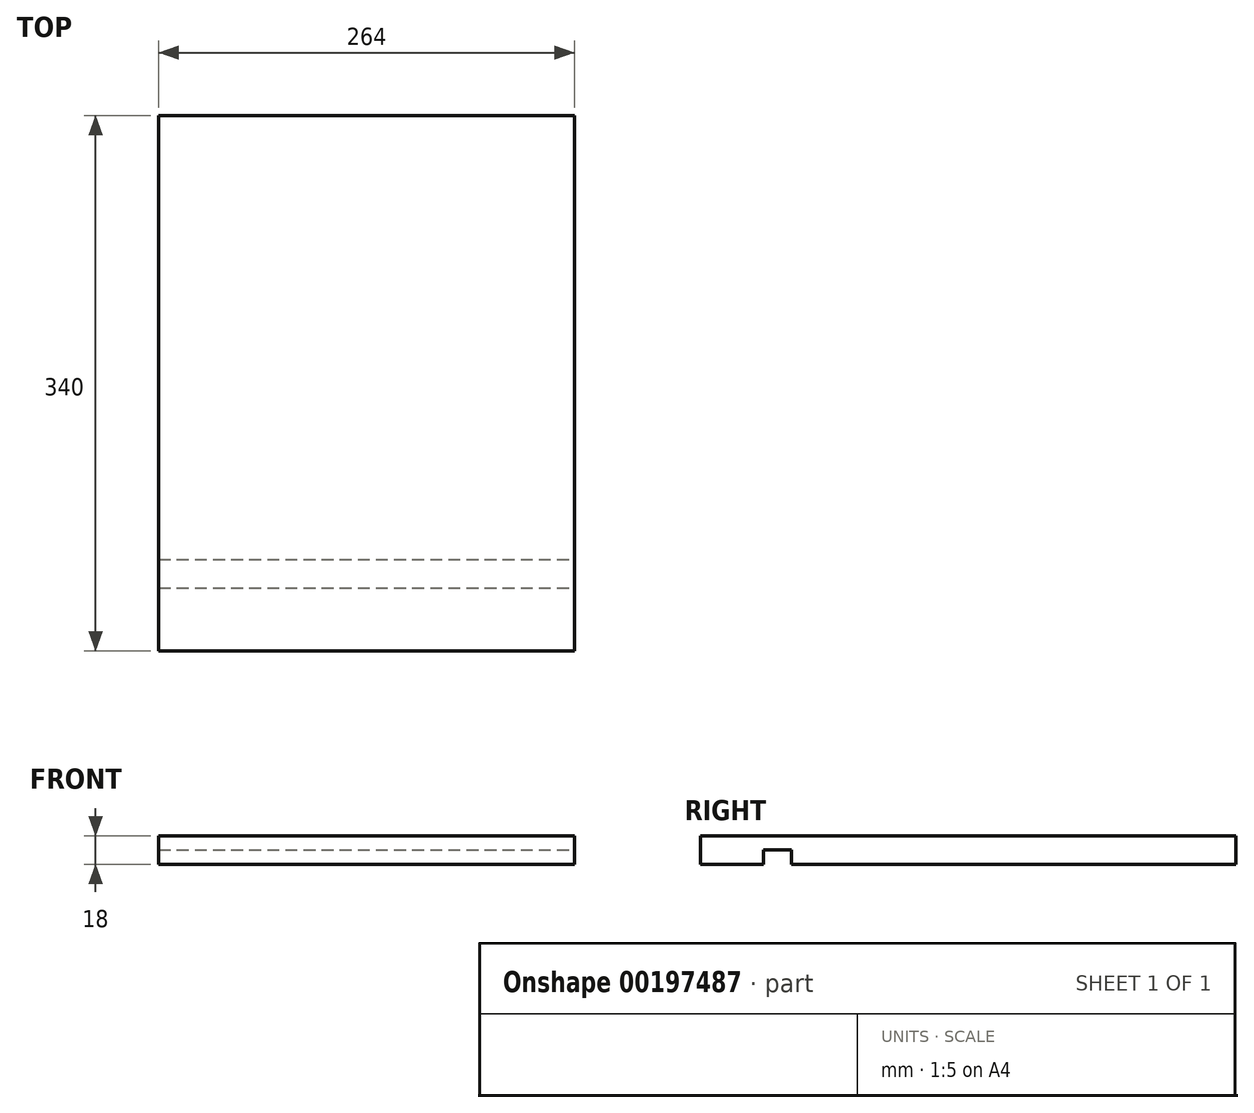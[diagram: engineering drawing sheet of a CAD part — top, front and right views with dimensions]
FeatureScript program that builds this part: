
annotation { "Feature Type Name" : "Feature", "Feature Type Description" : "" }
export const myFeature = defineFeature(function(context is Context, id is Id, definition is map)
    precondition{}
    {
        {
            var Q0;
            Q0=qCreatedBy(makeId("Top.planeOp"),FACE);
            var sketch = newSketch(context, id + "F0", { "sketchPlane" : qUnion([Q0])});
            skLineSegment(sketch, "E0.bottom", {"start": v(132, -170) * mm, "end": v(-132, -170) * mm});
            skLineSegment(sketch, "E0.top", {"start": v(132, 170) * mm, "end": v(-132, 170) * mm});
            skLineSegment(sketch, "E0.left", {"start": v(132, -170) * mm, "end": v(132, 170) * mm});
            skLineSegment(sketch, "E0.right", {"start": v(-132, -170) * mm, "end": v(-132, 170) * mm});
            skPoint(sketch, "E0.middle", {"position": v(0, 0) * mm});
            skSolve(sketch);
        }
        {
            var Q0;
            Q0=qSketchRegion(id+"F0",true);
            extrude(context, id + "F1", {"entities" : qUnion([Q0]), "depth" : 18 * mm});
        }
        {
            var Q0;
            Q0=makeQuery(id+"F1.opExtrude","CAP_FACE",FACE,{"disambiguationData":[OSD([sQuery(id+"F0.wireOp",EDGE,"E0.bottom"),sQuery(id+"F0.wireOp",EDGE,"E0.top"),sQuery(id+"F0.wireOp",EDGE,"E0.left"),sQuery(id+"F0.wireOp",EDGE,"E0.right")])],"isStart":true});
            var sketch = newSketch(context, id + "F2", { "sketchPlane" : qUnion([Q0])});
            skLineSegment(sketch, "E1.bottom", {"start": v(-132, 130) * mm, "end": v(132, 130) * mm});
            skLineSegment(sketch, "E1.top", {"start": v(-132, 112) * mm, "end": v(132, 112) * mm});
            skLineSegment(sketch, "E1.left", {"start": v(-132, 130) * mm, "end": v(-132, 112) * mm});
            skLineSegment(sketch, "E1.right", {"start": v(132, 130) * mm, "end": v(132, 112) * mm});
            skSolve(sketch);
        }
        {
            var Q0;
            Q0 = qSketchRegion(id + "F2", true);
            extrude(context, id + "F3", {"entities" : qUnion([Q0]), "operationType" : NewBodyOperationType.REMOVE, "oppositeDirection" : true, "depth" : 9 * mm});
        }
    });
